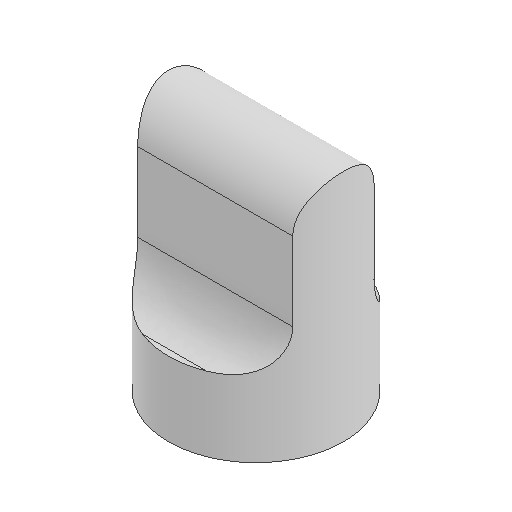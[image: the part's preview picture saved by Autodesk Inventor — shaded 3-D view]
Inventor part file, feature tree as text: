
AUTODESK INVENTOR PART (.ipt)
format: ipt  version: 2025 (Build 290162010, 162A)  size: 121,856 bytes
history: native  units: in
note: dims shown in document units (in); Inventor stores cm internally (conversion verified against a paired STEP export)
features: extrude x2, sketch x2
ambient origin geometry x8: Origin, YZ Plane, XZ Plane, XY Plane, X Axis, Y Axis, Z Axis, Center Point
bodies: Solid1 (feature_tree)
feature tree (4):
  extrude  "Extrusion1"  Depth=0.2in
  extrude  "Extrusion2"  Depth=0.1in
  sketch  "Sketch1"  dims[d0=0.2in d1=0.43in]
  sketch  "Sketch2"  dims[d2=0.575in d3=0.0in d4=0.1in d5=0.1in d6=0.575in d7=0.0in]
